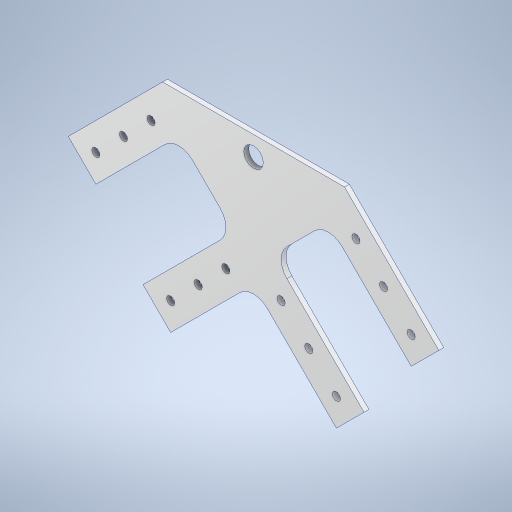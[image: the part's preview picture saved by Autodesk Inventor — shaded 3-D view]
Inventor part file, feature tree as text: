
AUTODESK INVENTOR PART (.ipt)
format: ipt  version: 2023 (Build 270158000, 158)  size: 333,824 bytes
history: native  units: in
note: dims shown in document units (in); Inventor stores cm internally (conversion verified against a paired STEP export)
features: extrude x2, sketch x2, other x1, mirror x1, fillet x1
ambient origin geometry x8: Origin, YZ Plane, XZ Plane, XY Plane, X Axis, Y Axis, Z Axis, Center Point
bodies: Solid1 (feature_tree)
feature tree (7):
  other  "<userpath>\OneDrive\Desktop\Robotics\URC Chassis Pivot\PivotParametersAndCalcs.xlsx"
  extrude  "Extrusion6"  Depth=1.0in
  extrude  "Extrusion7"  Depth=0.5in
  mirror  "Mirror3"
  fillet  "Fillet4"  Radius=0.5in
  sketch  "Sketch8"  dims[d108=0.5in d110=1.0in]
  sketch  "Sketch9"  dims[d111=3.0in d112=0.5in d113=0.5in d114=2.0in d115=135.0deg d116=0.125in d117=0.0in d119=45.0deg d120=0.5in d121=0.2087in d122=1.1811in d124=1.0in d125=0.3937in d127=1.0in d129=1.0in d130=0.0in d131=3.0in d133=1.0in d134=0.2087in d135=0.5in d136=1.1811in d138=1.0in d139=0.3937in d141=1.0in d143=0.5in]
